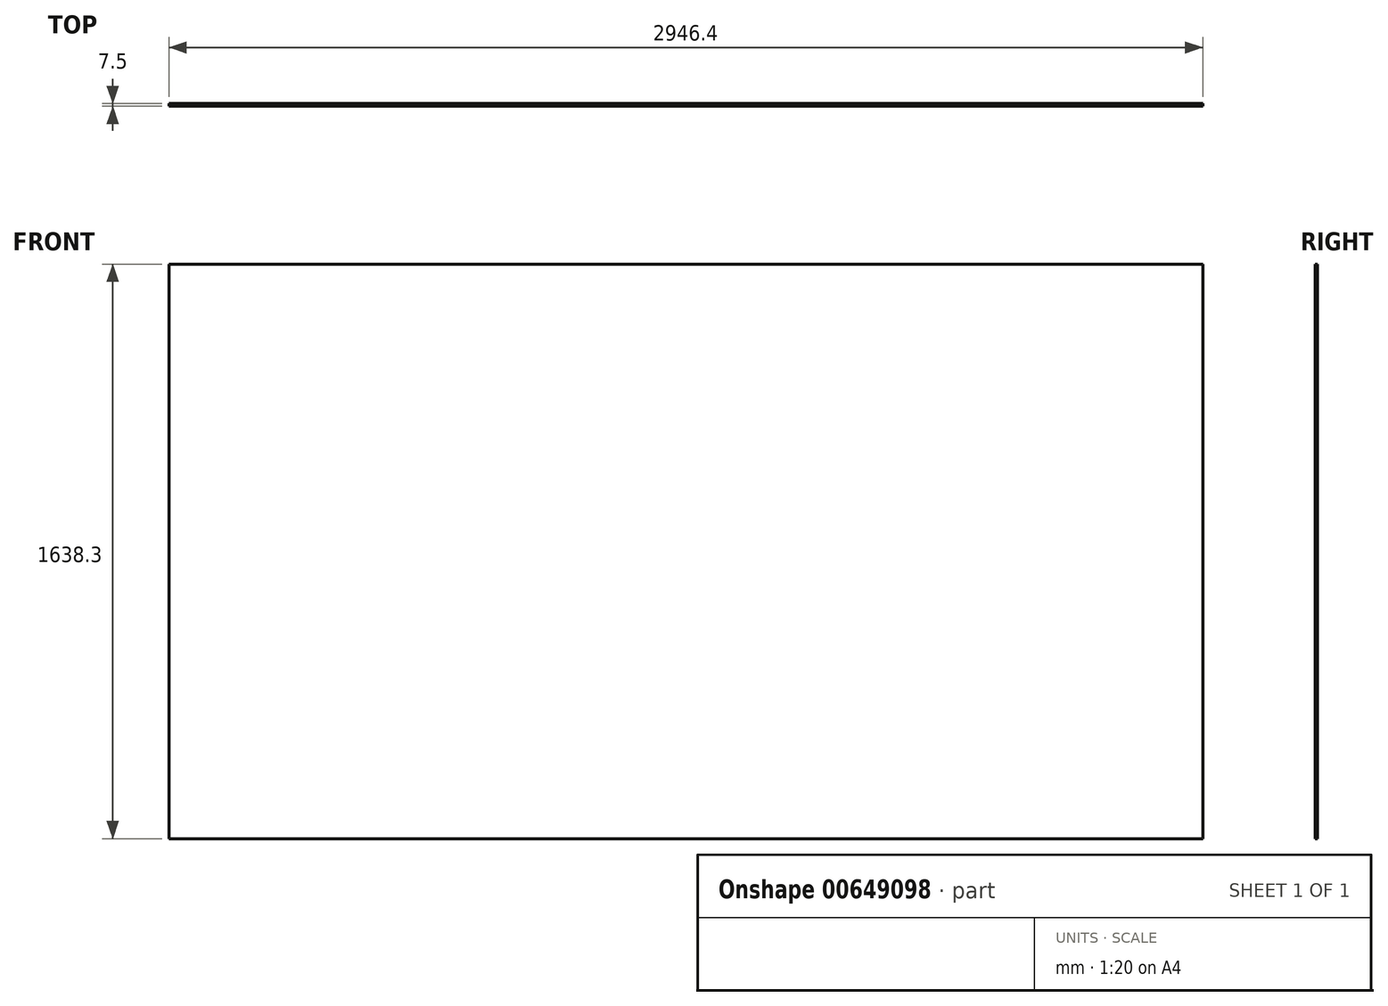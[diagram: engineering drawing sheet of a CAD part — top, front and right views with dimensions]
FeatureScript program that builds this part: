
annotation { "Feature Type Name" : "Feature", "Feature Type Description" : "" }
export const myFeature = defineFeature(function(context is Context, id is Id, definition is map)
    precondition{}
    {
        {
            var Q0;
            Q0=qCreatedBy(makeId("Front.planeOp"),FACE);
            var sketch = newSketch(context, id + "F0", { "sketchPlane" : qUnion([Q0])});
            skLineSegment(sketch, "E0.bottom", {"start": v(-1473.2, 819.15) * mm, "end": v(1473.2, 819.15) * mm});
            skLineSegment(sketch, "E0.top", {"start": v(-1473.2, -819.15) * mm, "end": v(1473.2, -819.15) * mm});
            skLineSegment(sketch, "E0.left", {"start": v(-1473.2, 819.15) * mm, "end": v(-1473.2, -819.15) * mm});
            skLineSegment(sketch, "E0.right", {"start": v(1473.2, 819.15) * mm, "end": v(1473.2, -819.15) * mm});
            skPoint(sketch, "E0.middle", {"position": v(0, 0) * mm});
            skSolve(sketch);
        }
        {
            var Q0;
            Q0=makeQuery(id+"F0.imprint","IMPRINT",FACE,{"disambiguationData":[TD([[makeQuery(id+"F0.imprint","IMPRINT",EDGE,{"derivedFrom":sQuery(id+"F0.wireOp",EDGE,"E0.bottom")}),-1.0]])]});
            extrude(context, id + "F1", {"entities" : qUnion([Q0]), "depth" : 7.5 * mm, "offsetDistance" : 25.4 * mm});
        }
    });
